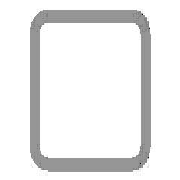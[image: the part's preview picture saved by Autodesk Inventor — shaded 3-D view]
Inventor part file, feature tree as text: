
AUTODESK INVENTOR PART (.ipt)
format: ipt  version: 2024 (Build 280153000, 153)  size: 143,872 bytes
history: native  units: mm (DEFAULTED — no unit token found)
features: other x4, plane x2, extrude x1, split x1, sketch x1
ambient origin geometry x8: Origin, YZ Plane, XZ Plane, XY Plane, X Axis, Y Axis, Z Axis, Center Point
bodies: Solid1 (feature_tree)
feature tree (9):
  parser-record x1  (decoder bookkeeping rows leaked as tree rows — omitted from the tree; the rows remain in map.json)
  other  "Driven Length"
  other  "Plano inicial"
  other  "Plano final"
  extrude  "Cuerpo"  TaperAngle=0.0deg  [1 undecoded]
  plane  "Plano de trabajo4"
  split  "Dividir1"
  sketch  "Sketch3"  dims[d3=525.4mm d4=0.0mm d10=50.8mm d11=50.8mm d12=3.175mm d13=-25.4mm d14=500.0mm d15=25.4mm d16=25.4mm d17=6.35mm d18=90.0deg d19=525.4mm]
  plane  "Work Plane3"
note: 1 required parameter value undecoded (feature->parameter linkage not recoverable at this tier; creation-order binding heuristic only, values carry confidence <= 0.55)
